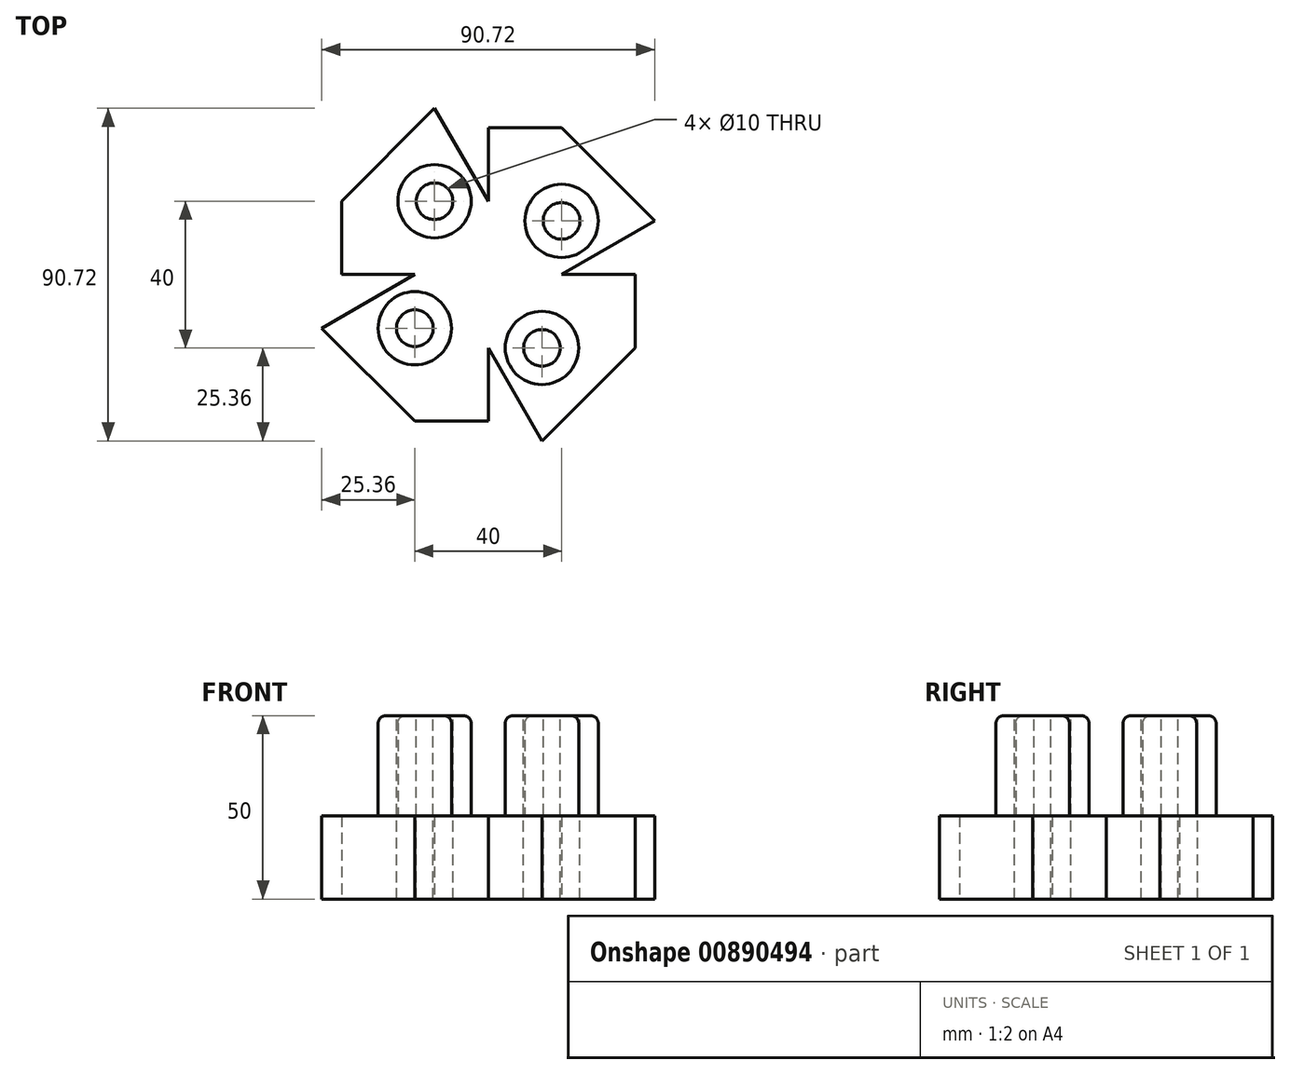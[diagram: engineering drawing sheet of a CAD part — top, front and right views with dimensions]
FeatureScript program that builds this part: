
annotation { "Feature Type Name" : "Feature", "Feature Type Description" : "" }
export const myFeature = defineFeature(function(context is Context, id is Id, definition is map)
    precondition{}
    {
        {
            var Q0;
            Q0=qCreatedBy(makeId("Top.planeOp"),FACE);
            var sketch = newSketch(context, id + "F0", { "sketchPlane" : qUnion([Q0])});
            skLineSegment(sketch, "E0", {"start": v(0, 0) * mm, "end": v(-40, 0) * mm});
            skLineSegment(sketch, "E1", {"start": v(-40, 0) * mm, "end": v(-40, 20) * mm});
            skLineSegment(sketch, "E2", {"start": v(-40, 20) * mm, "end": v(0, 20) * mm, "construction": true});
            skLineSegment(sketch, "E3", {"start": v(0, 20) * mm, "end": v(0, 0) * mm});
            skLineSegment(sketch, "E4", {"start": v(-40, 20) * mm, "end": v(-14.64, 45.36) * mm});
            skLineSegment(sketch, "E5", {"start": v(0, 20) * mm, "end": v(-14.64, 45.36) * mm});
            skLineSegment(sketch, "E6", {"start": v(-14.64, 45.36) * mm, "end": v(-14.64, 0) * mm, "construction": true});
            skCircle(sketch, "E7", {"center": v(-14.64, 20) * mm, "radius": 10 * mm});
            skArc(sketch, "E8", {"start": v(-17.22, 29.66) * mm, "mid": v(-33.65, 18.7) * mm, "end": v(-40, 0) * mm});
            skLineSegment(sketch, "E9.1.0", {"start": v(-45.36, -14.64) * mm, "end": v(0, -14.64) * mm, "construction": true});
            skLineSegment(sketch, "E9.1.1", {"start": v(0, 0) * mm, "end": v(0, -40) * mm});
            skLineSegment(sketch, "E9.1.2", {"start": v(0, -40) * mm, "end": v(-20, -40) * mm});
            skCircle(sketch, "E9.1.3", {"center": v(-20, -14.64) * mm, "radius": 10 * mm});
            skArc(sketch, "E9.1.4", {"start": v(-29.66, -17.22) * mm, "mid": v(-18.7, -33.65) * mm, "end": v(0, -40) * mm});
            skLineSegment(sketch, "E9.1.5", {"start": v(-20, -40) * mm, "end": v(-45.36, -14.64) * mm});
            skLineSegment(sketch, "E9.1.6", {"start": v(-20, -40) * mm, "end": v(-20, 0) * mm, "construction": true});
            skLineSegment(sketch, "E9.1.7", {"start": v(-20, 0) * mm, "end": v(0, 0) * mm});
            skLineSegment(sketch, "E9.1.8", {"start": v(-20, 0) * mm, "end": v(-45.36, -14.64) * mm});
            skLineSegment(sketch, "E9.2.0", {"start": v(14.64, -45.36) * mm, "end": v(14.64, 0) * mm, "construction": true});
            skLineSegment(sketch, "E9.2.1", {"start": v(0, 0) * mm, "end": v(40, 0) * mm});
            skLineSegment(sketch, "E9.2.2", {"start": v(40, 0) * mm, "end": v(40, -20) * mm});
            skCircle(sketch, "E9.2.3", {"center": v(14.64, -20) * mm, "radius": 10 * mm});
            skArc(sketch, "E9.2.4", {"start": v(17.22, -29.66) * mm, "mid": v(33.65, -18.7) * mm, "end": v(40, 0) * mm});
            skLineSegment(sketch, "E9.2.5", {"start": v(40, -20) * mm, "end": v(14.64, -45.36) * mm});
            skLineSegment(sketch, "E9.2.6", {"start": v(40, -20) * mm, "end": v(0, -20) * mm, "construction": true});
            skLineSegment(sketch, "E9.2.7", {"start": v(0, -20) * mm, "end": v(0, 0) * mm});
            skLineSegment(sketch, "E9.2.8", {"start": v(0, -20) * mm, "end": v(14.64, -45.36) * mm});
            skLineSegment(sketch, "E9.3.0", {"start": v(45.36, 14.64) * mm, "end": v(0, 14.64) * mm, "construction": true});
            skLineSegment(sketch, "E9.3.1", {"start": v(0, 0) * mm, "end": v(0, 40) * mm});
            skLineSegment(sketch, "E9.3.2", {"start": v(0, 40) * mm, "end": v(20, 40) * mm});
            skCircle(sketch, "E9.3.3", {"center": v(20, 14.64) * mm, "radius": 10 * mm});
            skArc(sketch, "E9.3.4", {"start": v(29.66, 17.22) * mm, "mid": v(18.7, 33.65) * mm, "end": v(0, 40) * mm});
            skLineSegment(sketch, "E9.3.5", {"start": v(20, 40) * mm, "end": v(45.36, 14.64) * mm});
            skLineSegment(sketch, "E9.3.6", {"start": v(20, 40) * mm, "end": v(20, 0) * mm, "construction": true});
            skLineSegment(sketch, "E9.3.7", {"start": v(20, 0) * mm, "end": v(0, 0) * mm});
            skLineSegment(sketch, "E9.3.8", {"start": v(20, 0) * mm, "end": v(45.36, 14.64) * mm});
            skPoint(sketch, "E9.center", {"position": v(0, 0) * mm});
            skSolve(sketch);
        }
        {
            var Q0;
            Q0=makeQuery(id+"F0.imprint","IMPRINT",FACE,{"disambiguationData":[TD([[makeQuery(id+"F0.imprint","IMPRINT",EDGE,{"derivedFrom":sQuery(id+"F0.wireOp",EDGE,"E9.1.1")}),-1.0]])]});
            var Q1;
            Q1=makeQuery(id+"F0.imprint","IMPRINT",FACE,{"disambiguationData":[TD([[makeQuery(id+"F0.imprint","IMPRINT",EDGE,{"derivedFrom":sQuery(id+"F0.wireOp",EDGE,"E0")}),-1.0]])]});
            var Q2;
            Q2=makeQuery(id+"F0.imprint","IMPRINT",FACE,{"disambiguationData":[TD([[makeQuery(id+"F0.imprint","IMPRINT",EDGE,{"derivedFrom":sQuery(id+"F0.wireOp",EDGE,"E7")}),1.0]])]});
            var Q3;
            Q3=makeQuery(id+"F0.imprint","IMPRINT",FACE,{"disambiguationData":[TD([[makeQuery(id+"F0.imprint","IMPRINT",EDGE,{"derivedFrom":sQuery(id+"F0.wireOp",EDGE,"E9.1.3")}),1.0]])]});
            var Q4;
            {var subQ0=sQuery(id+"F0.wireOp",EDGE,"E9.3.2");Q4=makeQuery(id+"F0.imprint","IMPRINT",FACE,{"disambiguationData":[TD([[makeQuery(id+"F0.imprint","IMPRINT",EDGE,{"derivedFrom":subQ0}),-1.0]])]});}
            var Q5;
            Q5=makeQuery(id+"F0.imprint","IMPRINT",FACE,{"disambiguationData":[TD([[makeQuery(id+"F0.imprint","IMPRINT",EDGE,{"derivedFrom":sQuery(id+"F0.wireOp",EDGE,"E9.2.3")}),1.0]])]});
            var Q6;
            Q6=makeQuery(id+"F0.imprint","IMPRINT",FACE,{"disambiguationData":[TD([[makeQuery(id+"F0.imprint","IMPRINT",EDGE,{"derivedFrom":sQuery(id+"F0.wireOp",EDGE,"E9.3.3")}),1.0]])]});
            var Q7;
            Q7=makeQuery(id+"F0.imprint","IMPRINT",FACE,{"disambiguationData":[TD([[makeQuery(id+"F0.imprint","IMPRINT",EDGE,{"derivedFrom":sQuery(id+"F0.wireOp",EDGE,"E9.2.1")}),-1.0]])]});
            extrude(context, id + "F1", {"entities" : qUnion([Q0, Q1, Q2, Q3, Q4, Q5, Q6, Q7]), "depth" : 22.7 * mm, "offsetDistance" : 25 * mm});
        }
        {
            var Q0;
            Q0=makeQuery(id+"F0.imprint","IMPRINT",FACE,{"disambiguationData":[TD([[makeQuery(id+"F0.imprint","IMPRINT",EDGE,{"derivedFrom":sQuery(id+"F0.wireOp",EDGE,"E9.1.3")}),1.0]])]});
            var Q1;
            Q1=makeQuery(id+"F0.imprint","IMPRINT",FACE,{"disambiguationData":[TD([[makeQuery(id+"F0.imprint","IMPRINT",EDGE,{"derivedFrom":sQuery(id+"F0.wireOp",EDGE,"E7")}),1.0]])]});
            var Q2;
            Q2=makeQuery(id+"F0.imprint","IMPRINT",FACE,{"disambiguationData":[TD([[makeQuery(id+"F0.imprint","IMPRINT",EDGE,{"derivedFrom":sQuery(id+"F0.wireOp",EDGE,"E9.3.3")}),1.0]])]});
            var Q3;
            Q3=makeQuery(id+"F0.imprint","IMPRINT",FACE,{"disambiguationData":[TD([[makeQuery(id+"F0.imprint","IMPRINT",EDGE,{"derivedFrom":sQuery(id+"F0.wireOp",EDGE,"E9.2.3")}),1.0]])]});
            extrude(context, id + "F2", {"entities" : qUnion([Q0, Q1, Q2, Q3]), "operationType" : NewBodyOperationType.ADD, "depth" : 50 * mm, "offsetDistance" : 25 * mm});
        }
        {
            var Q0;
            Q0=makeQuery(id+"F2.opExtrude","CAP_FACE",FACE,{"disambiguationData":[OSD([sQuery(id+"F0.wireOp",EDGE,"E7")])],"isStart":false});
            var sketch = newSketch(context, id + "F3", { "sketchPlane" : qUnion([Q0])});
            skCircle(sketch, "E10", {"center": v(20, 14.64) * mm, "radius": 5 * mm});
            skSolve(sketch);
        }
        {
            var Q0;
            Q0=makeQuery(id+"F3.imprint","IMPRINT",FACE,{"disambiguationData":[TD([[makeQuery(id+"F3.imprint","IMPRINT",EDGE,{"derivedFrom":makeQuery(id+"F2.opExtrude","CAP_EDGE",EDGE,{"disambiguationData":[OSD([sQuery(id+"F0.wireOp",EDGE,"E7")])],"isStart":false})}),1.0]])]});
            var sketch = newSketch(context, id + "F4", { "sketchPlane" : qUnion([Q0])});
            skCircle(sketch, "E11", {"center": v(-14.64, 20) * mm, "radius": 5 * mm});
            skCircle(sketch, "E12", {"center": v(-20, -14.64) * mm, "radius": 5 * mm});
            skCircle(sketch, "E13", {"center": v(14.64, -20) * mm, "radius": 5 * mm});
            skSolve(sketch);
        }
        {
            var Q0;
            Q0=makeQuery(id+"F3.imprint","IMPRINT",FACE,{"disambiguationData":[TD([[makeQuery(id+"F3.imprint","IMPRINT",EDGE,{"derivedFrom":sQuery(id+"F3.wireOp",EDGE,"E10")}),1.0]])]});
            extrude(context, id + "F5", {"entities" : qUnion([Q0]), "operationType" : NewBodyOperationType.REMOVE, "oppositeDirection" : true, "depth" : 50 * mm, "offsetDistance" : 25 * mm});
        }
        {
            var Q0;
            Q0=makeQuery(id+"F3.imprint","IMPRINT",FACE,{"disambiguationData":[TD([[makeQuery(id+"F3.imprint","IMPRINT",EDGE,{"derivedFrom":sQuery(id+"F3.wireOp",EDGE,"E10")}),1.0]])]});
            var Q1;
            Q1=makeQuery(id+"F4.imprint","IMPRINT",FACE,{"disambiguationData":[TD([[makeQuery(id+"F4.imprint","IMPRINT",EDGE,{"derivedFrom":sQuery(id+"F4.wireOp",EDGE,"E11")}),1.0]])]});
            var Q2;
            Q2=makeQuery(id+"F4.imprint","IMPRINT",FACE,{"disambiguationData":[TD([[makeQuery(id+"F4.imprint","IMPRINT",EDGE,{"derivedFrom":sQuery(id+"F4.wireOp",EDGE,"E12")}),1.0]])]});
            var Q3;
            Q3=makeQuery(id+"F4.imprint","IMPRINT",FACE,{"disambiguationData":[TD([[makeQuery(id+"F4.imprint","IMPRINT",EDGE,{"derivedFrom":sQuery(id+"F4.wireOp",EDGE,"E13")}),1.0]])]});
            extrude(context, id + "F6", {"entities" : qUnion([Q0, Q1, Q2, Q3]), "operationType" : NewBodyOperationType.REMOVE, "oppositeDirection" : true, "depth" : 50 * mm, "offsetDistance" : 25 * mm});
        }
        {
            var Q0;
            Q0=makeQuery(id+"F2.opExtrude","CAP_EDGE",EDGE,{"disambiguationData":[OSD([sQuery(id+"F0.wireOp",EDGE,"E9.1.3")])],"isStart":false});
            var Q1;
            Q1=makeQuery(id+"F2.opExtrude","CAP_EDGE",EDGE,{"disambiguationData":[OSD([sQuery(id+"F0.wireOp",EDGE,"E9.2.3")])],"isStart":false});
            var Q2;
            Q2=makeQuery(id+"F2.opExtrude","CAP_EDGE",EDGE,{"disambiguationData":[OSD([sQuery(id+"F0.wireOp",EDGE,"E9.3.3")])],"isStart":false});
            var Q3;
            Q3=makeQuery(id+"F2.opExtrude","CAP_EDGE",EDGE,{"disambiguationData":[OSD([sQuery(id+"F0.wireOp",EDGE,"E7")])],"isStart":false});
            fillet(context, id + "F7", {"entities" : qUnion([Q0, Q1, Q2, Q3]), "radius" : 2 * mm, "tangentPropagation" : true, "allowEdgeOverflow" : false});
        }
    });
